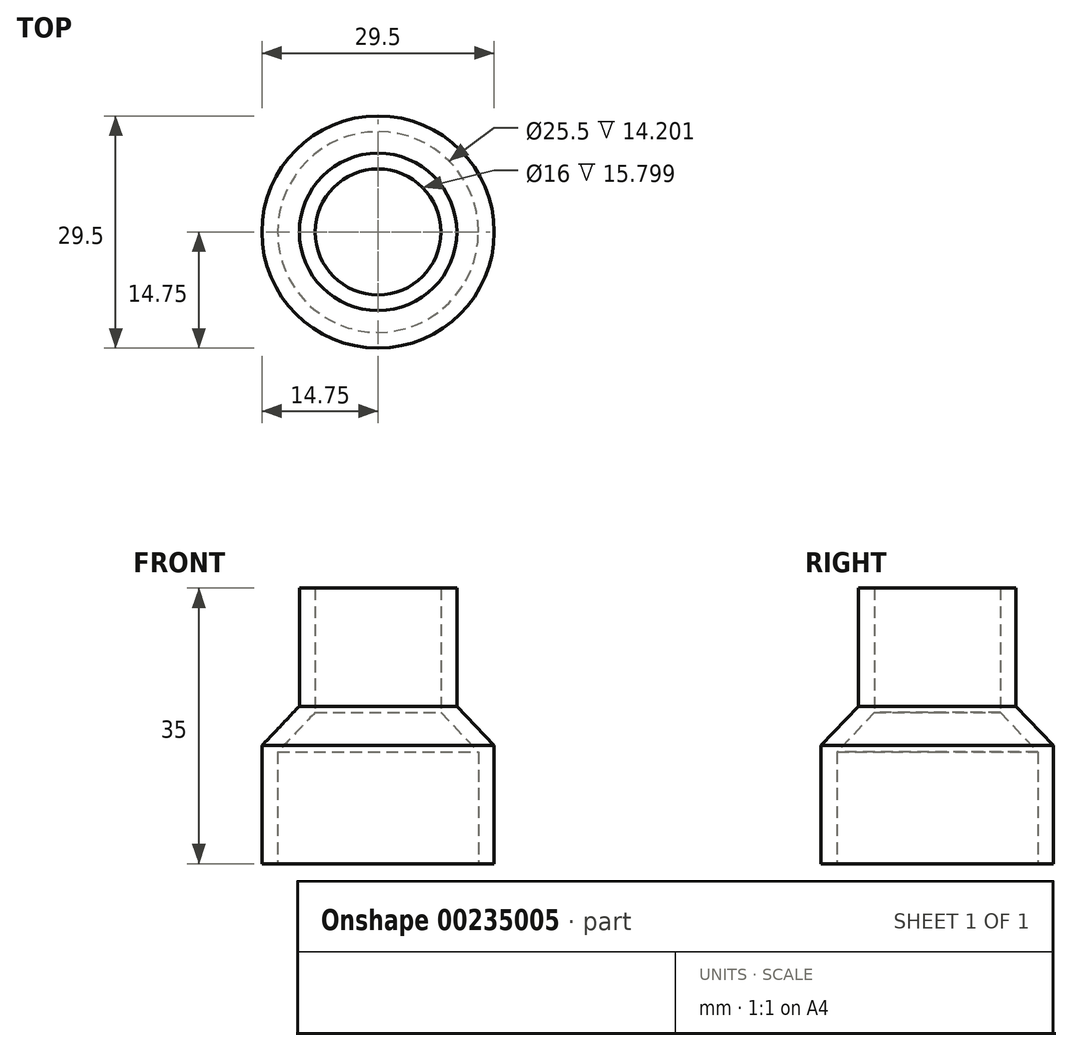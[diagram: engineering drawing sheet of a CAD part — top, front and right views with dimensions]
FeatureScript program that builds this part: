
annotation { "Feature Type Name" : "Feature", "Feature Type Description" : "" }
export const myFeature = defineFeature(function(context is Context, id is Id, definition is map)
    precondition{}
    {
        {
            var Q0;
            Q0=qCreatedBy(makeId("Right.planeOp"),FACE);
            var sketch = newSketch(context, id + "F0", { "sketchPlane" : qUnion([Q0])});
            skLineSegment(sketch, "E0", {"start": v(12.75, 0) * mm, "end": v(14.75, 0) * mm});
            skLineSegment(sketch, "E1", {"start": v(14.75, 0) * mm, "end": v(14.75, 15) * mm});
            skLineSegment(sketch, "E2", {"start": v(14.75, 15) * mm, "end": v(10, 20) * mm});
            skLineSegment(sketch, "E3", {"start": v(10, 20) * mm, "end": v(10, 35) * mm});
            skLineSegment(sketch, "E4", {"start": v(10, 35) * mm, "end": v(8, 35) * mm});
            skLineSegment(sketch, "E5", {"start": v(8, 35) * mm, "end": v(8, 19.2) * mm});
            skLineSegment(sketch, "E6", {"start": v(8, 19.2) * mm, "end": v(12.75, 14.2) * mm});
            skLineSegment(sketch, "E7", {"start": v(12.75, 14.2) * mm, "end": v(12.75, 0) * mm});
            skLineSegment(sketch, "E8", {"start": v(0, 0) * mm, "end": v(0, 13.85) * mm, "construction": true});
            skSolve(sketch);
        }
        {
            var Q0;
            Q0 = qSketchRegion(id + "F0", true);
            var Q1;
            Q1=sQuery(id+"F0.wireOp",EDGE,"E8");
            revolve(context, id + "F1", {"entities" : qUnion([Q0]), "axis" : qUnion([Q1]), "revolveType" : RevolveType.FULL});
        }
    });
